# Revit family: Water_Heaters_HAJDU_HAJDU-STXL-400C-500C_
name_source: partatom
category: Mechanical Equipment
units: mm (PartAtom-declared; Revit-internal decimal feet)

## family parameters
Always vertical = Yes
Classification = None
Cut with Voids When Loaded = No
Maintain Annotation Orientation = No
OmniClass Number = 23.31.29.13
OmniClass Title = Hot Water Tank Heaters
Part Type = Normal
Room Calculation Point = No
Round Connector Dimension = Use Diameter
Shared = No
Work Plane-Based = Yes

## types (2) — shared parameters
Case Material = Hajdu - Felület - Fehér
Csatlakozó magassága "A" = 320 mm  [stored 1.04987 ft]
Default Elevation = 1219.2 mm  [stored 4 ft]
Description = A nagy teljesítményű tárolók, amelyek alkalmasak bármilyen hőtermelő eszközzel való felfűtésre, de a nagy felületű hőcserélőjüknek köszönhetően különösen célszerűek kondenzációs kazánokhoz és alacsony hőmérsékletű fűtési rendszerekhez. Nem rendelkezik különálló fűtőbetéttel de utólagosan is van lehetőség a behelyezésére, mely által használati melegvizet biztosítanak kazán vagy napkollektor nélkül is. A nagy teljesítményű, STXL típusú tartályokat kifejezetten hőszivattyús rendszerekhez ajánljuk.
Elektromos futopatron csatlakozás = 38.1 mm  [stored 0.125 ft]
Eltolt = 30 mm  [stored 0.0984252 ft]
Energiahatékonysági osztály = B
Hocserélo csatlakozás = 31.75 mm
Homéro csonk = 12.7 mm  [stored 0.0416667 ft]
Manufacturer = HAJDU
Product Page URL = https://hajdurt.hu
Top Anód = Yes
URL = https://hajdurt.hu
Vízcsatlakozás = 25.4 mm  [stored 0.0833333 ft]
lábak = Yes
Érintésvédelmi osztály = I.
Érzékelo tokcso = 12.7 mm  [stored 0.0416667 ft]
Üzemi nyomás = 1.0 MPa

## per-type parameters (varying)
| type | Csatlakozó magassága "B" | Csatlakozó magassága "C" | Csatlakozó magassága "E" | Csatlakozó magassága "F" | Csatlakozó magassága "G" | Csatlakozó magassága "I" | Církulációs csonk | Hocserélo felulete | Hocserélo névleges urtartalma | Hocserélo tartós teljesítmény | Magasság | Névleges urtartalom | Rádiusz | Tárolási veszteség | Tömeg | Átméro |
| STXL 400C | 1000 mm  [stored 3.28084 ft] | 1260 mm  [stored 4.13386 ft] | 1525 mm  [stored 5.00328 ft] | 345 mm  [stored 1.13189 ft] | 1521 mm  [stored 4.99016 ft] | 1330 mm  [stored 4.36352 ft] | 19.05 mm  [stored 0.0625 ft] | 5 m2 | 35 l | 150 kW | 1800 mm  [stored 5.90551 ft] | 400 l | 340 mm  [stored 1.11549 ft] | 73.3 W | 212.00 kg | 680 mm  [stored 2.23097 ft] |
| STXL 500C | 1040 mm  [stored 3.41207 ft] | 1290 mm  [stored 4.23228 ft] | 1500 mm  [stored 4.92126 ft] | 370 mm  [stored 1.21391 ft] | 1498 mm  [stored 4.9147 ft] | 1360 mm  [stored 4.46194 ft] | 25.4 mm  [stored 0.0833333 ft] | 6 m2 | 42 l | 180 kW | 1806 mm  [stored 5.9252 ft] | 500 l | 380 mm  [stored 1.24672 ft] | 79.2 W | 254.00 kg | 760 mm |

note: column(s) folded — value = type name in every type: Model

note: [stored X ft] marks values corroborated as IEEE doubles in the binary element streams (Revit-internal decimal feet)

## geometry (parser evidence)
native form markers: Sweep x5
no freeform markers — native parametric forms only
